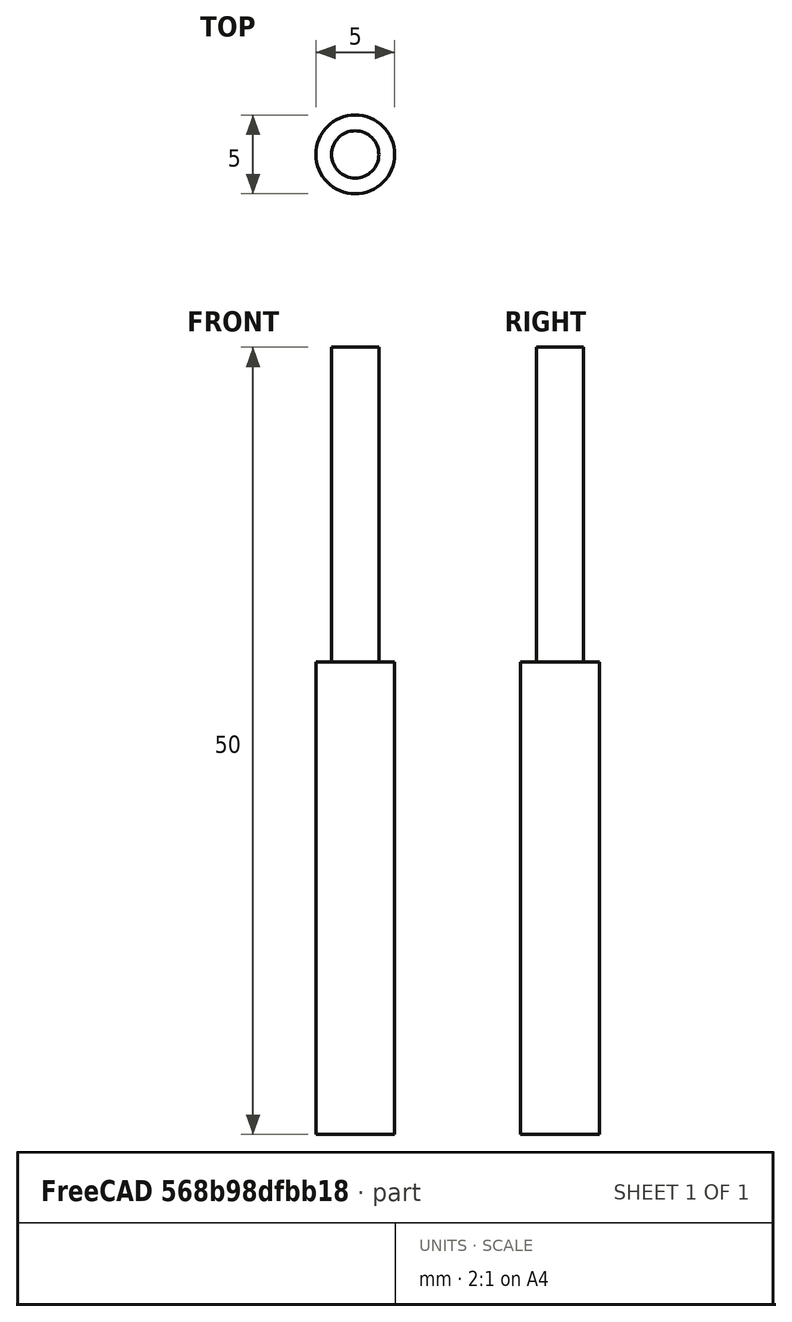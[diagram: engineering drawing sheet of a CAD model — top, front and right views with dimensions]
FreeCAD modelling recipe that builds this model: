
FCSTD DOCUMENT  (FreeCAD 0.19R20874 (Git))
Label: endmill
License: All rights reserved
LicenseURL: http://en.wikipedia.org/wiki/All_rights_reserved
objects: Sketcher::SketchObject×1, PartDesign::Revolution×1, PartDesign::Body×1
note: 4 computed .brp shape members not serialized (recipe doc carries the construction recipe); baked Part::Feature solids carry a one-line shape summary decoded from their .brp

FEATURE [Sketcher::SketchObject] Sketch
  MapMode = 5
  Placement = pos=(0,0,0) rot=(1,0,0;1.5708rad)
  Support = -> [XZ_Plane]
  sketch-geometry (8):
    g0: LineSegment StartX=0 StartY=50 StartZ=0 EndX=0 EndY=0 EndZ=0
    g1: LineSegment StartX=0 StartY=0 StartZ=0 EndX=2.5 EndY=0 EndZ=0
    g2: LineSegment StartX=2.5 StartY=0 StartZ=0 EndX=2.5 EndY=30 EndZ=0
    g3: LineSegment StartX=1.5 StartY=50 StartZ=0 EndX=0 EndY=50 EndZ=0
    g4: LineSegment [constr] StartX=2.5 StartY=0 StartZ=0 EndX=-2.5 EndY=0 EndZ=0
    g5: LineSegment StartX=1.5 StartY=30 StartZ=0 EndX=2.5 EndY=30 EndZ=0
    g6: LineSegment StartX=1.5 StartY=50 StartZ=0 EndX=1.5 EndY=30 EndZ=0
    g7: LineSegment [constr] StartX=-1.5 StartY=50 StartZ=0 EndX=1.5 EndY=50 EndZ=0
  constraints (21):
    c: Vertical(g0)
    c: Coincident(g0,g1)
    c: Horizontal(g1)
    c: Coincident(g1,g2)
    c: Vertical(g2)
    c: Horizontal(g3)
    c: Coincident(g0,g3)
    c: Coincident(g4,g1)
    c: Symmetric(g1,g4,g0)
    c: DistanceX(g4,g4) = 5  'Diameter; Endmill diameter'
    c: DistanceY(g2,g3) = 50  'Length; Overall length of the endmill'
    c: Horizontal(g5)
    c: Coincident(g2,g5)
    c: Vertical(g6)
    c: Coincident(g3,g6)
    c: Symmetric(g7,g7,g0)
    c: Coincident(g7,g3)
    c: DistanceX(g7,g7) = 3  'ShankDiameter; diameter of the shank'
    c: Coincident(g5,g6)
    c: DistanceY(g2) = 30  'CuttingEdgeHeight'
    c: Coincident(g0,g-1)
FEATURE [PartDesign::Revolution] Revolution
  AllowMultiFace = false
  Angle = 360
  Axis = (0,-2e-16,1)
  Base = (0,0,0)
  Placement = pos=(0,0,0) rot=(1,0,0;1.5708rad)
  Profile = -> Sketch
  ReferenceAxis = -> Sketch [V_Axis]
  Reversed = true
FEATURE [PartDesign::Body] Body  label="Endmill"
  Group = -> [Sketch,Revolution]
  Origin = -> Origin
  Tip = -> Revolution
